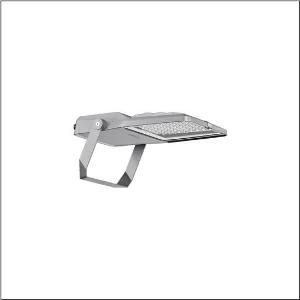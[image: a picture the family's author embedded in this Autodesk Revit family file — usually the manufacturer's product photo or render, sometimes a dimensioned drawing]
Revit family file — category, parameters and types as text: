
# Revit family: floodlight_fl_21_iq_mini___pl33t_5xa7772d4f1a_39e2
name_source: partatom
category: Lighting Fixtures
units: mm (PartAtom-declared; Revit-internal decimal feet)

## family parameters
Cut with Voids When Loaded = No
Host = Face
Light Source = No
Part Type = Normal
Room Calculation Point = No
Round Connector Dimension = Use Diameter
Shared = No

## types (1)
- --- (1 x LED, 18390 lm, 143 W, 4000K)
    Apparent Load = 143 VA
    CIE Flux Codes = 26 75 99 100 100
    Color Rendering = 70
    Color Temperature = 4000K
    Default Elevation = 1800 mm
    Description = Floodlight FL 21 iQ mini, floodlight, primary light control with lens, of PMMA, primary optical cover: protective disc, of toughened safety glass, transparent, light distribution: PL33T, light emission: direct distribution, installation type: surface-mounted, LED, High Power LED, rated luminous flux: 18.390lm, luminous efficacy: 129lm/W, light colour: 740, colour temperature: 4000K, control: Street-Remote, Auto-Match, Temp-Guard, Night-Set, Smart-Wire, Desk-Remote (wireless, voltage-free reading and setting of iQ features in the workshop via application-optimized NFC function/RFID function), optimised constant luminous flux control (CLO 2.0), with terminal, 6-pole, mains connection: 220..240V, AC, 50/60Hz, start of lifetime: 143W, end of service life: 152W, reduction: 61W, luminaire housing, of diecast aluminium, powder-coated, Siteco® metallic grey (DB 702S), corrosivity category C5 mid according to DIN EN ISO 12944, sealing non-destructively replaceable, mounting bracket, of steel, galvanised, powder-coated, Siteco® metallic grey (DB 702S), protection rating (complete): IP66, insulation class (complete): insulation class II (safety insulation), certification: CE, ENEC, VDE, protection symbol: D, impact resistance: IK08, permissible operating ambient temperature: -40..+40°C, permissible operating ambient temperature for outdoor applications: -40..+50°C, standard: DIN EN 12944, LABS conformity tested according to VDMA 24364:2018-05, packaging unit: 1 piece

Light Distribution: PL33T
    Height = 70 mm
    Lamp = 1 x LED
    Lamp Light Flux = 18390 lm
    Lamp Power = 143 W
    Lamp count = 1
    Length = 485 mm
    Luminous efficacy = 129 lm/W
    Manufacturer = Siteco
    ModVariant = No
    Model = 5XA7772D4F1A
    Number of Poles = 1
    OnlyDefault = Yes
    Power Factor = 1
    Product Name = Floodlight FL 21 iQ mini | PL33T
    Product group = floodlight | pylon annexe
    ProductGroupID = 6200
    Protection Class = Protection class II
    Protection Degree = IP 66
    RLX_Detail_Level = 1
    RLX_Emergency_Light_Flux = 0 lm
    RLX_Emergency_Type = 0
    RLX_Emergency_Type_DB = No
    RlxData = <blob elided: 96389 chars, md5=ea5a5ca7>
    Socket = socket
    Standby Power = 0 W
    System Light Flux = 18390 lm
    System Power = 143 W
    Type Comments = factory setting: luminous flux: 100 % | dim-lin: 254 | 730 mA
    Type Image = l_1006845.jpg
    URL = http://relux.com
    VarID = @adj_081339
    Voltage = 0 V
    Weight = 0.00 kg
    Width = 337 mm

## geometry (parser evidence)
native form markers: Blend x4, Sweep x11
no freeform markers — native parametric forms only
